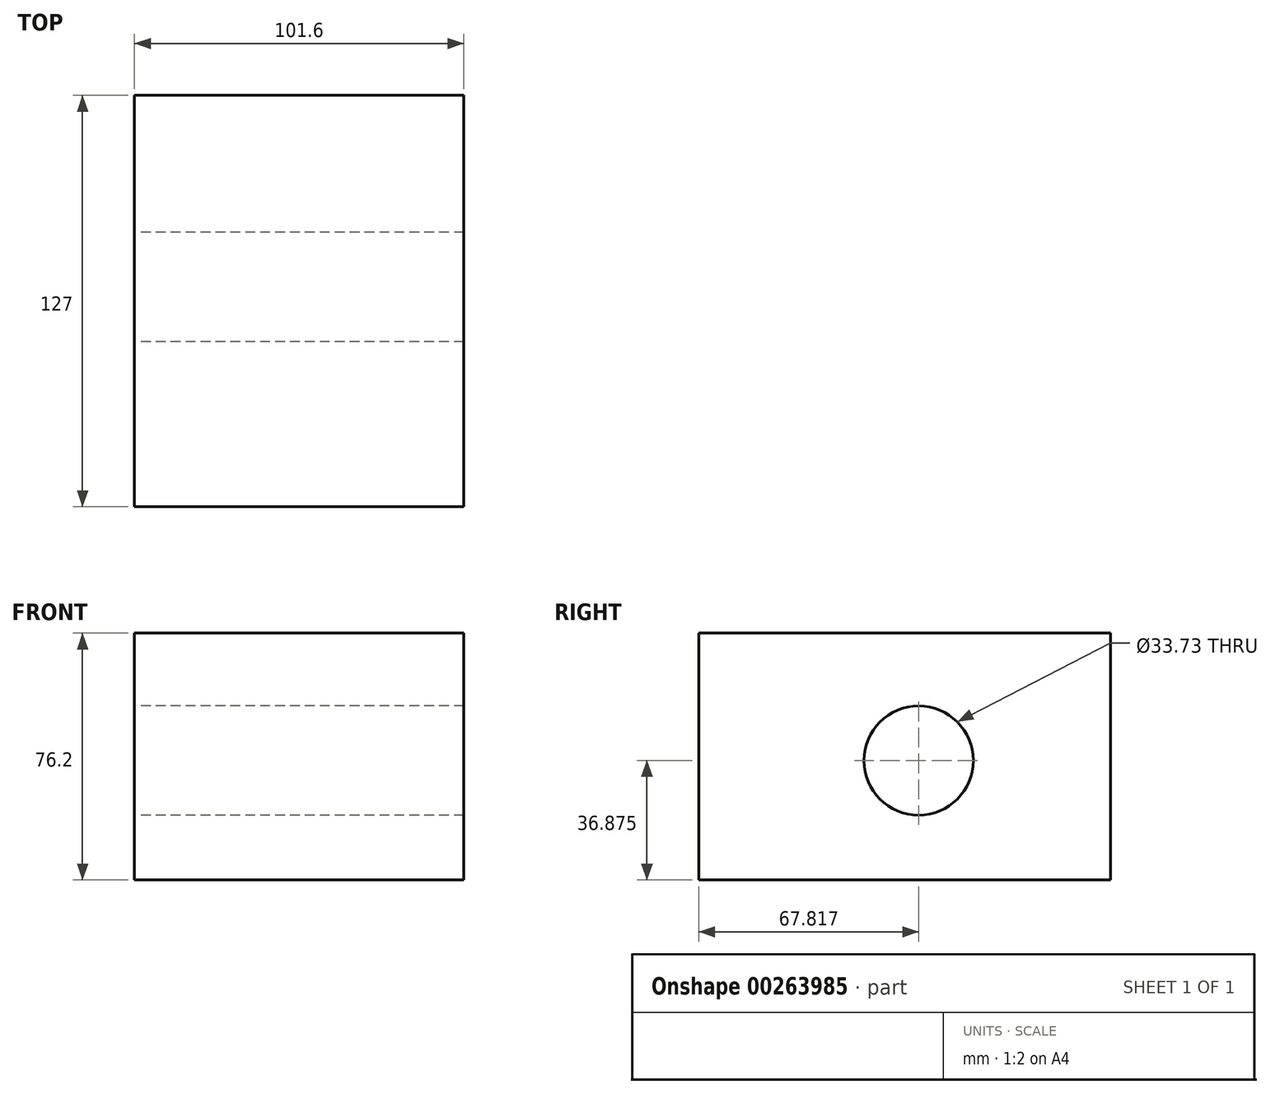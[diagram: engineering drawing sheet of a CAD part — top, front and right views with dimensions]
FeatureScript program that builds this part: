
annotation { "Feature Type Name" : "Feature", "Feature Type Description" : "" }
export const myFeature = defineFeature(function(context is Context, id is Id, definition is map)
    precondition{}
    {
        {
            var Q0;
            Q0=qCreatedBy(makeId("Front.planeOp"),FACE);
            var sketch = newSketch(context, id + "F0", { "sketchPlane" : qUnion([Q0])});
            skLineSegment(sketch, "E0.bottom", {"start": v(0, 0) * mm, "end": v(101.6, 0) * mm});
            skLineSegment(sketch, "E0.top", {"start": v(0, 76.2) * mm, "end": v(101.6, 76.2) * mm});
            skLineSegment(sketch, "E0.left", {"start": v(0, 0) * mm, "end": v(0, 76.2) * mm});
            skLineSegment(sketch, "E0.right", {"start": v(101.6, 0) * mm, "end": v(101.6, 76.2) * mm});
            skSolve(sketch);
        }
        {
            var Q0;
            Q0=makeQuery(id+"F0.imprint","IMPRINT",FACE,{"disambiguationData":[TD([[makeQuery(id+"F0.imprint","IMPRINT",EDGE,{"derivedFrom":sQuery(id+"F0.wireOp",EDGE,"E0.bottom")}),1.0]])]});
            extrude(context, id + "F1", {"entities" : qUnion([Q0]), "oppositeDirection" : true, "depth" : 127 * mm});
        }
        {
            var Q0;
            Q0=makeQuery(id+"F1.opExtrude","SWEPT_FACE",FACE,{"disambiguationData":[OSD([sQuery(id+"F0.wireOp",EDGE,"E0.left")])]});
            var sketch = newSketch(context, id + "F2", { "sketchPlane" : qUnion([Q0])});
            skCircle(sketch, "E1", {"center": v(-67.82, 36.87) * mm, "radius": 16.87 * mm});
            skSolve(sketch);
        }
        {
            var Q0;
            Q0=makeQuery(id+"F2.imprint","IMPRINT",FACE,{"disambiguationData":[TD([[makeQuery(id+"F2.imprint","IMPRINT",EDGE,{"derivedFrom":sQuery(id+"F2.wireOp",EDGE,"E1")}),1.0]])]});
            extrude(context, id + "F3", {"entities" : qUnion([Q0]), "operationType" : NewBodyOperationType.REMOVE, "endBound" : BoundingType.UP_TO_NEXT, "oppositeDirection" : true, "depth" : 127 * mm});
        }
    });
